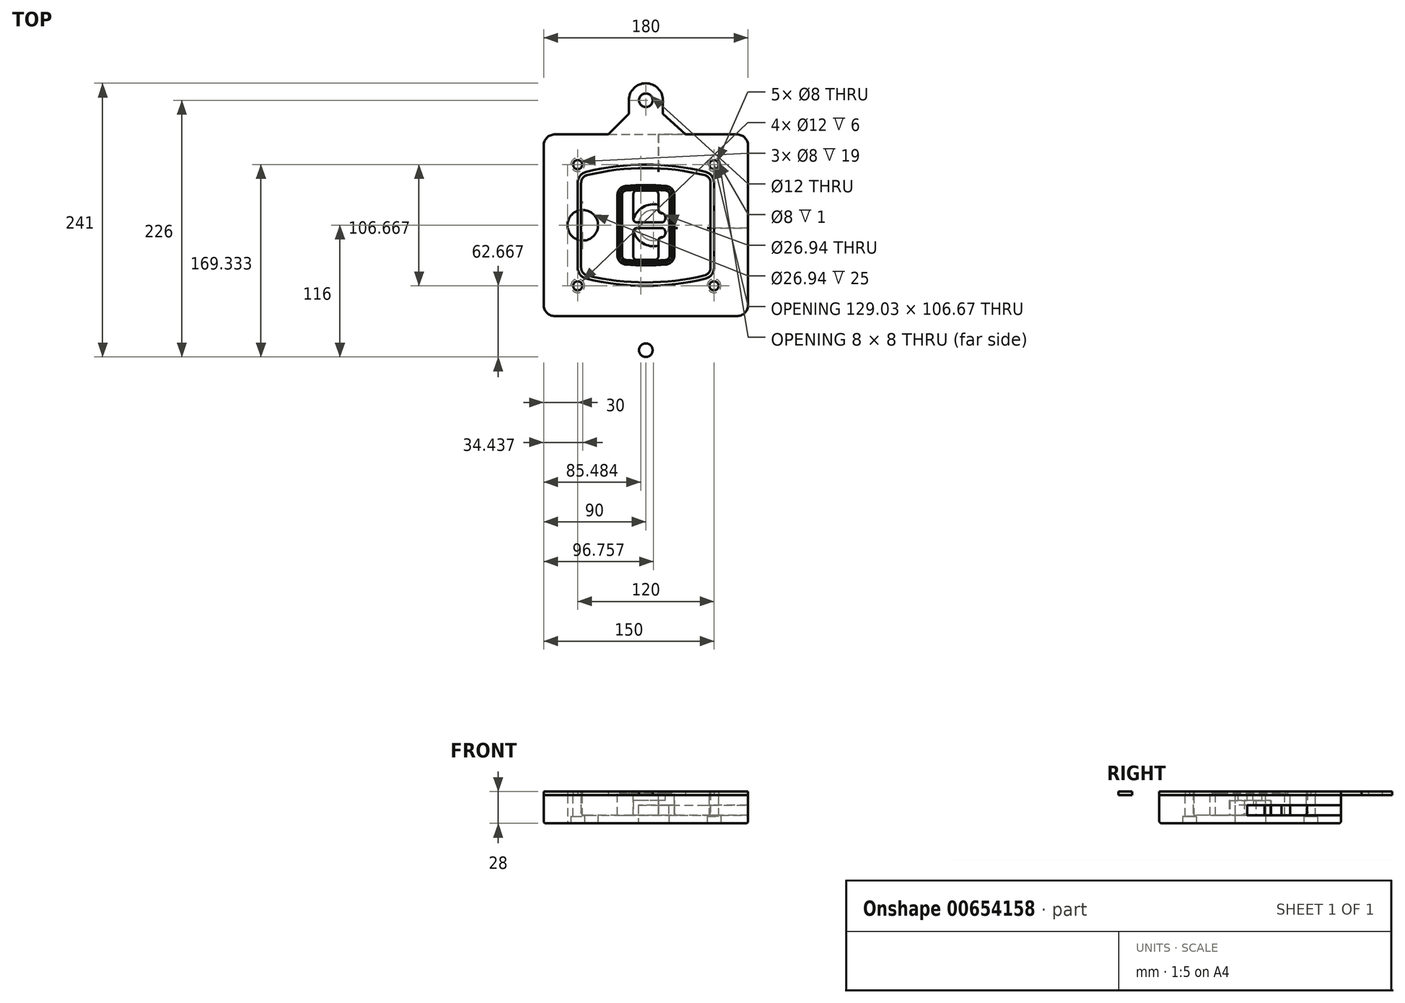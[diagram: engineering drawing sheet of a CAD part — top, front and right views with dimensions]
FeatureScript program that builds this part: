
annotation { "Feature Type Name" : "Feature", "Feature Type Description" : "" }
export const myFeature = defineFeature(function(context is Context, id is Id, definition is map)
    precondition{}
    {
        {
            var Q0;
            Q0=qCreatedBy(makeId("Top.planeOp"),FACE);
            var sketch = newSketch(context, id + "F0", { "sketchPlane" : qUnion([Q0])});
            skPoint(sketch, "E0.rect.middle", {"position": v(0, 0) * mm});
            skLineSegment(sketch, "E1.bottom", {"start": v(-80, -80) * mm, "end": v(80, -80) * mm});
            skLineSegment(sketch, "E1.top", {"start": v(-80, 80) * mm, "end": v(80, 80) * mm});
            skLineSegment(sketch, "E1.left", {"start": v(-90, -70) * mm, "end": v(-90, 70) * mm});
            skLineSegment(sketch, "E1.right", {"start": v(90, -70) * mm, "end": v(90, 70) * mm});
            skLineSegment(sketch, "E2", {"start": v(-90, 80) * mm, "end": v(90, -80) * mm, "construction": true});
            skLineSegment(sketch, "E3", {"start": v(90, 80) * mm, "end": v(-90, -80) * mm, "construction": true});
            skCircle(sketch, "E4", {"center": v(-60, 53.33) * mm, "radius": 4 * mm});
            skCircle(sketch, "E5", {"center": v(60, 53.33) * mm, "radius": 4 * mm});
            skCircle(sketch, "E6", {"center": v(60, -53.33) * mm, "radius": 4 * mm});
            skCircle(sketch, "E7", {"center": v(-60, -53.33) * mm, "radius": 4 * mm});
            skLineSegment(sketch, "E8", {"start": v(-60, 53.33) * mm, "end": v(60, 53.33) * mm, "construction": true});
            skLineSegment(sketch, "E9", {"start": v(60, 53.33) * mm, "end": v(60, -53.33) * mm, "construction": true});
            skLineSegment(sketch, "E10", {"start": v(60, -53.33) * mm, "end": v(-60, -53.33) * mm, "construction": true});
            skLineSegment(sketch, "E11", {"start": v(-60, -53.33) * mm, "end": v(-60, 53.33) * mm, "construction": true});
            skLineSegment(sketch, "E12", {"start": v(-60, 37.3) * mm, "end": v(-60, -37.3) * mm});
            skLineSegment(sketch, "E13", {"start": v(60, 37.3) * mm, "end": v(60, -37.3) * mm});
            skArc(sketch, "E14", {"start": v(52.38, 47.01) * mm, "mid": v(0, 53.33) * mm, "end": v(-52.38, 47.01) * mm});
            skArc(sketch, "E15", {"start": v(-52.38, -47.01) * mm, "mid": v(0, -53.33) * mm, "end": v(52.38, -47.01) * mm});
            skLineSegment(sketch, "E16", {"start": v(-60, 0) * mm, "end": v(60, 0) * mm, "construction": true});
            skPoint(sketch, "E17.visualSharp", {"position": v(-60, -45) * mm});
            skArc(sketch, "E17.filletArc", {"start": v(-60, -37.3) * mm, "mid": v(-57.87, -43.47) * mm, "end": v(-52.38, -47.01) * mm});
            skPoint(sketch, "E18.visualSharp", {"position": v(-60, 45) * mm});
            skArc(sketch, "E18.filletArc", {"start": v(-52.38, 47.01) * mm, "mid": v(-57.87, 43.47) * mm, "end": v(-60, 37.3) * mm});
            skPoint(sketch, "E19.visualSharp", {"position": v(60, 45) * mm});
            skArc(sketch, "E19.filletArc", {"start": v(60, 37.3) * mm, "mid": v(57.87, 43.47) * mm, "end": v(52.38, 47.01) * mm});
            skPoint(sketch, "E20.visualSharp", {"position": v(60, -45) * mm});
            skArc(sketch, "E20.filletArc", {"start": v(52.38, -47.01) * mm, "mid": v(57.87, -43.47) * mm, "end": v(60, -37.3) * mm});
            skPoint(sketch, "E21.visualSharp", {"position": v(-90, 80) * mm});
            skArc(sketch, "E21.filletArc", {"start": v(-80, 80) * mm, "mid": v(-87.07, 77.07) * mm, "end": v(-90, 70) * mm});
            skPoint(sketch, "E22.visualSharp", {"position": v(90, 80) * mm});
            skArc(sketch, "E22.filletArc", {"start": v(90, 70) * mm, "mid": v(87.07, 77.07) * mm, "end": v(80, 80) * mm});
            skPoint(sketch, "E23.visualSharp", {"position": v(90, -80) * mm});
            skArc(sketch, "E23.filletArc", {"start": v(80, -80) * mm, "mid": v(87.07, -77.07) * mm, "end": v(90, -70) * mm});
            skPoint(sketch, "E24.visualSharp", {"position": v(-90, -80) * mm});
            skArc(sketch, "E24.filletArc", {"start": v(-90, -70) * mm, "mid": v(-87.07, -77.07) * mm, "end": v(-80, -80) * mm});
            skArc(sketch, "E25.0", {"start": v(57, 37.3) * mm, "mid": v(55.5, 41.62) * mm, "end": v(51.67, 44.1) * mm});
            skLineSegment(sketch, "E25.1", {"start": v(57, 37.3) * mm, "end": v(57, -37.3) * mm});
            skArc(sketch, "E25.2", {"start": v(51.67, -44.1) * mm, "mid": v(55.5, -41.62) * mm, "end": v(57, -37.3) * mm});
            skArc(sketch, "E25.3", {"start": v(-51.67, -44.1) * mm, "mid": v(0, -50.33) * mm, "end": v(51.67, -44.1) * mm});
            skArc(sketch, "E25.4", {"start": v(-57, -37.3) * mm, "mid": v(-55.5, -41.62) * mm, "end": v(-51.67, -44.1) * mm});
            skArc(sketch, "E25.5", {"start": v(51.67, 44.1) * mm, "mid": v(0, 50.33) * mm, "end": v(-51.67, 44.1) * mm});
            skLineSegment(sketch, "E25.6", {"start": v(-57, 37.3) * mm, "end": v(-57, -37.3) * mm});
            skArc(sketch, "E25.7", {"start": v(-51.67, 44.1) * mm, "mid": v(-55.5, 41.62) * mm, "end": v(-57, 37.3) * mm});
            skArc(sketch, "E26.0", {"start": v(-53.33, 50.9) * mm, "mid": v(-61.01, 45.94) * mm, "end": v(-64, 37.3) * mm});
            skArc(sketch, "E26.1", {"start": v(53.33, 50.9) * mm, "mid": v(0, 57.33) * mm, "end": v(-53.33, 50.9) * mm});
            skArc(sketch, "E26.2", {"start": v(64, 37.3) * mm, "mid": v(61.01, 45.94) * mm, "end": v(53.33, 50.9) * mm});
            skLineSegment(sketch, "E26.3", {"start": v(64, 37.3) * mm, "end": v(64, -37.3) * mm});
            skArc(sketch, "E26.4", {"start": v(53.33, -50.9) * mm, "mid": v(61.01, -45.94) * mm, "end": v(64, -37.3) * mm});
            skLineSegment(sketch, "E26.5", {"start": v(-64, 37.3) * mm, "end": v(-64, -37.3) * mm});
            skArc(sketch, "E26.6", {"start": v(-53.33, -50.9) * mm, "mid": v(0, -57.33) * mm, "end": v(53.33, -50.9) * mm});
            skArc(sketch, "E26.7", {"start": v(-64, -37.3) * mm, "mid": v(-61.01, -45.94) * mm, "end": v(-53.33, -50.9) * mm});
            skSolve(sketch);
        }
        {
            var Q0;
            Q0=makeQuery(id+"F0.imprint","IMPRINT",FACE,{"disambiguationData":[TD([[makeQuery(id+"F0.imprint","IMPRINT",EDGE,{"derivedFrom":sQuery(id+"F0.wireOp",EDGE,"E1.bottom")}),1.0]])]});
            var Q1;
            Q1=makeQuery(id+"F0.imprint","IMPRINT",FACE,{"disambiguationData":[TD([[makeQuery(id+"F0.imprint","IMPRINT",EDGE,{"derivedFrom":sQuery(id+"F0.wireOp",EDGE,"E12")}),1.0]])]});
            var Q2;
            Q2=makeQuery(id+"F0.imprint","IMPRINT",FACE,{"disambiguationData":[TD([[makeQuery(id+"F0.imprint","IMPRINT",EDGE,{"derivedFrom":sQuery(id+"F0.wireOp",EDGE,"E25.0")}),1.0]])]});
            var Q3;
            Q3=makeQuery(id+"F0.imprint","IMPRINT",FACE,{"disambiguationData":[TD([[makeQuery(id+"F0.imprint","IMPRINT",EDGE,{"derivedFrom":sQuery(id+"F0.wireOp",EDGE,"E12")}),-1.0]])]});
            extrude(context, id + "F1", {"entities" : qUnion([Q0, Q1, Q2, Q3]), "oppositeDirection" : true, "depth" : 25 * mm});
        }
        {
            var Q0;
            Q0=makeQuery(id+"F0.imprint","IMPRINT",FACE,{"disambiguationData":[TD([[makeQuery(id+"F0.imprint","IMPRINT",EDGE,{"derivedFrom":sQuery(id+"F0.wireOp",EDGE,"E12")}),1.0]])]});
            extrude(context, id + "F2", {"entities" : qUnion([Q0]), "operationType" : NewBodyOperationType.ADD, "depth" : 3 * mm});
        }
        {
            var Q0;
            Q0=makeQuery(id+"F0.imprint","IMPRINT",FACE,{"disambiguationData":[TD([[makeQuery(id+"F0.imprint","IMPRINT",EDGE,{"derivedFrom":sQuery(id+"F0.wireOp",EDGE,"E25.0")}),1.0]])]});
            extrude(context, id + "F3", {"entities" : qUnion([Q0]), "operationType" : NewBodyOperationType.REMOVE, "oppositeDirection" : true, "depth" : 18 * mm});
        }
        {
            var Q0;
            Q0=makeQuery(id+"F2.opExtrude","CAP_FACE",FACE,{"disambiguationData":[OSD([sQuery(id+"F0.wireOp",EDGE,"E12"),sQuery(id+"F0.wireOp",EDGE,"E13"),sQuery(id+"F0.wireOp",EDGE,"E14"),sQuery(id+"F0.wireOp",EDGE,"E15"),sQuery(id+"F0.wireOp",EDGE,"E17.filletArc"),sQuery(id+"F0.wireOp",EDGE,"E18.filletArc"),sQuery(id+"F0.wireOp",EDGE,"E19.filletArc"),sQuery(id+"F0.wireOp",EDGE,"E20.filletArc"),sQuery(id+"F0.wireOp",EDGE,"E25.0"),sQuery(id+"F0.wireOp",EDGE,"E25.1"),sQuery(id+"F0.wireOp",EDGE,"E25.2"),sQuery(id+"F0.wireOp",EDGE,"E25.3"),sQuery(id+"F0.wireOp",EDGE,"E25.4"),sQuery(id+"F0.wireOp",EDGE,"E25.5"),sQuery(id+"F0.wireOp",EDGE,"E25.6"),sQuery(id+"F0.wireOp",EDGE,"E25.7")])],"isStart":false});
            var sketch = newSketch(context, id + "F4", { "sketchPlane" : qUnion([Q0])});
            skArc(sketch, "E27.0", {"start": v(-17.7, -34.56) * mm, "mid": v(0, -35.33) * mm, "end": v(17.7, -34.56) * mm});
            skArc(sketch, "E28.0", {"start": v(17.7, 34.56) * mm, "mid": v(0, 35.33) * mm, "end": v(-17.7, 34.56) * mm});
            skLineSegment(sketch, "E29", {"start": v(-25, 26.59) * mm, "end": v(-25, -26.59) * mm});
            skLineSegment(sketch, "E30", {"start": v(25, 26.59) * mm, "end": v(25, -26.59) * mm});
            skLineSegment(sketch, "E31", {"start": v(-25, 33.78) * mm, "end": v(25, 33.78) * mm, "construction": true});
            skLineSegment(sketch, "E32", {"start": v(-25, -33.78) * mm, "end": v(25, -33.78) * mm, "construction": true});
            skPoint(sketch, "E33.visualSharp", {"position": v(-25, 33.78) * mm});
            skArc(sketch, "E33.filletArc", {"start": v(-17.7, 34.56) * mm, "mid": v(-22.9, 32) * mm, "end": v(-25, 26.59) * mm});
            skPoint(sketch, "E34.visualSharp", {"position": v(25, 33.78) * mm});
            skArc(sketch, "E34.filletArc", {"start": v(25, 26.59) * mm, "mid": v(22.9, 32) * mm, "end": v(17.7, 34.56) * mm});
            skPoint(sketch, "E35.visualSharp", {"position": v(25, -33.78) * mm});
            skArc(sketch, "E35.filletArc", {"start": v(17.7, -34.56) * mm, "mid": v(22.9, -32) * mm, "end": v(25, -26.59) * mm});
            skPoint(sketch, "E36.visualSharp", {"position": v(-25, -33.78) * mm});
            skArc(sketch, "E36.filletArc", {"start": v(-25, -26.59) * mm, "mid": v(-22.9, -32) * mm, "end": v(-17.7, -34.56) * mm});
            skArc(sketch, "E37.0", {"start": v(51.67, 44.1) * mm, "mid": v(0, 50.33) * mm, "end": v(-51.67, 44.1) * mm});
            skArc(sketch, "E37.1", {"start": v(-51.67, 44.1) * mm, "mid": v(-55.5, 41.62) * mm, "end": v(-57, 37.3) * mm});
            skLineSegment(sketch, "E37.2", {"start": v(-57, 37.3) * mm, "end": v(-57, -37.3) * mm});
            skArc(sketch, "E37.3", {"start": v(-57, -37.3) * mm, "mid": v(-55.5, -41.62) * mm, "end": v(-51.67, -44.1) * mm});
            skArc(sketch, "E37.4", {"start": v(-51.67, -44.1) * mm, "mid": v(0, -50.33) * mm, "end": v(51.67, -44.1) * mm});
            skArc(sketch, "E37.5", {"start": v(51.67, -44.1) * mm, "mid": v(55.5, -41.62) * mm, "end": v(57, -37.3) * mm});
            skLineSegment(sketch, "E37.6", {"start": v(57, 37.3) * mm, "end": v(57, -37.3) * mm});
            skArc(sketch, "E37.7", {"start": v(57, 37.3) * mm, "mid": v(55.5, 41.62) * mm, "end": v(51.67, 44.1) * mm});
            skLineSegment(sketch, "E38.0", {"start": v(23, 26.59) * mm, "end": v(23, -26.59) * mm});
            skArc(sketch, "E38.1", {"start": v(17.53, -32.56) * mm, "mid": v(21.42, -30.64) * mm, "end": v(23, -26.59) * mm});
            skArc(sketch, "E38.2", {"start": v(-17.53, -32.56) * mm, "mid": v(0, -33.33) * mm, "end": v(17.53, -32.56) * mm});
            skArc(sketch, "E38.3", {"start": v(-23, -26.59) * mm, "mid": v(-21.42, -30.64) * mm, "end": v(-17.53, -32.56) * mm});
            skLineSegment(sketch, "E38.4", {"start": v(-23, 26.59) * mm, "end": v(-23, -26.59) * mm});
            skArc(sketch, "E38.5", {"start": v(23, 26.59) * mm, "mid": v(21.42, 30.64) * mm, "end": v(17.53, 32.56) * mm});
            skArc(sketch, "E38.6", {"start": v(-17.53, 32.56) * mm, "mid": v(-21.42, 30.64) * mm, "end": v(-23, 26.59) * mm});
            skArc(sketch, "E38.7", {"start": v(17.53, 32.56) * mm, "mid": v(0, 33.33) * mm, "end": v(-17.53, 32.56) * mm});
            skArc(sketch, "E39.0", {"start": v(21, 26.59) * mm, "mid": v(19.95, 29.29) * mm, "end": v(17.35, 30.57) * mm});
            skLineSegment(sketch, "E39.1", {"start": v(21, 26.59) * mm, "end": v(21, -26.59) * mm});
            skArc(sketch, "E39.2", {"start": v(17.35, -30.57) * mm, "mid": v(19.95, -29.29) * mm, "end": v(21, -26.59) * mm});
            skArc(sketch, "E39.3", {"start": v(-17.35, -30.57) * mm, "mid": v(0, -31.33) * mm, "end": v(17.35, -30.57) * mm});
            skArc(sketch, "E39.4", {"start": v(-21, -26.59) * mm, "mid": v(-19.95, -29.29) * mm, "end": v(-17.35, -30.57) * mm});
            skArc(sketch, "E39.5", {"start": v(17.35, 30.57) * mm, "mid": v(0, 31.33) * mm, "end": v(-17.35, 30.57) * mm});
            skLineSegment(sketch, "E39.6", {"start": v(-21, 26.59) * mm, "end": v(-21, -26.59) * mm});
            skArc(sketch, "E39.7", {"start": v(-17.35, 30.57) * mm, "mid": v(-19.95, 29.29) * mm, "end": v(-21, 26.59) * mm});
            skLineSegment(sketch, "E40", {"start": v(-25, 0) * mm, "end": v(25, 0) * mm, "construction": true});
            skLineSegment(sketch, "E41", {"start": v(-11, 5.5) * mm, "end": v(-11, 27.5) * mm});
            skLineSegment(sketch, "E42", {"start": v(-8, 30.5) * mm, "end": v(8, 30.5) * mm});
            skLineSegment(sketch, "E43", {"start": v(11, 27.5) * mm, "end": v(11, 13.5) * mm});
            skLineSegment(sketch, "E44", {"start": v(14, 10.5) * mm, "end": v(14, 10.5) * mm});
            skLineSegment(sketch, "E45", {"start": v(17, 7.5) * mm, "end": v(17, 5.5) * mm});
            skLineSegment(sketch, "E46", {"start": v(14, 2.5) * mm, "end": v(-8, 2.5) * mm});
            skPoint(sketch, "E47.visualSharp", {"position": v(-11, 30.5) * mm});
            skArc(sketch, "E47.filletArc", {"start": v(-8, 30.5) * mm, "mid": v(-10.12, 29.62) * mm, "end": v(-11, 27.5) * mm});
            skPoint(sketch, "E48.visualSharp", {"position": v(11, 30.5) * mm});
            skArc(sketch, "E48.filletArc", {"start": v(11, 27.5) * mm, "mid": v(10.12, 29.62) * mm, "end": v(8, 30.5) * mm});
            skPoint(sketch, "E49.visualSharp", {"position": v(11, 10.5) * mm});
            skArc(sketch, "E49.filletArc", {"start": v(11, 13.5) * mm, "mid": v(11.88, 11.38) * mm, "end": v(14, 10.5) * mm});
            skPoint(sketch, "E50.visualSharp", {"position": v(17, 10.5) * mm});
            skArc(sketch, "E50.filletArc", {"start": v(17, 7.5) * mm, "mid": v(16.12, 9.62) * mm, "end": v(14, 10.5) * mm});
            skPoint(sketch, "E51.visualSharp", {"position": v(17, 2.5) * mm});
            skArc(sketch, "E51.filletArc", {"start": v(14, 2.5) * mm, "mid": v(16.12, 3.38) * mm, "end": v(17, 5.5) * mm});
            skPoint(sketch, "E52.visualSharp", {"position": v(-11, 2.5) * mm});
            skArc(sketch, "E52.filletArc", {"start": v(-11, 5.5) * mm, "mid": v(-10.12, 3.38) * mm, "end": v(-8, 2.5) * mm});
            skLineSegment(sketch, "E53.0.MirrorCS", {"start": v(14, -2.5) * mm, "end": v(-8, -2.5) * mm});
            skArc(sketch, "E54.0.MirrorCS", {"start": v(-11, -5.5) * mm, "mid": v(-10.12, -3.38) * mm, "end": v(-8, -2.5) * mm});
            skLineSegment(sketch, "E55.0.MirrorCS", {"start": v(-11, -5.5) * mm, "end": v(-11, -27.5) * mm});
            skArc(sketch, "E56.0.MirrorCS", {"start": v(-8, -30.5) * mm, "mid": v(-10.12, -29.62) * mm, "end": v(-11, -27.5) * mm});
            skLineSegment(sketch, "E57.0.MirrorCS", {"start": v(-8, -30.5) * mm, "end": v(8, -30.5) * mm});
            skArc(sketch, "E58.0.MirrorCS", {"start": v(11, -27.5) * mm, "mid": v(10.12, -29.62) * mm, "end": v(8, -30.5) * mm});
            skLineSegment(sketch, "E59.0.MirrorCS", {"start": v(11, -27.5) * mm, "end": v(11, -13.5) * mm});
            skArc(sketch, "E60.0.MirrorCS", {"start": v(11, -13.5) * mm, "mid": v(11.88, -11.38) * mm, "end": v(14, -10.5) * mm});
            skArc(sketch, "E61.0.MirrorCS", {"start": v(17, -7.5) * mm, "mid": v(16.12, -9.62) * mm, "end": v(14, -10.5) * mm});
            skLineSegment(sketch, "E62.0.MirrorCS", {"start": v(17, -7.5) * mm, "end": v(17, -5.5) * mm});
            skArc(sketch, "E63.0.MirrorCS", {"start": v(14, -2.5) * mm, "mid": v(16.12, -3.38) * mm, "end": v(17, -5.5) * mm});
            skSolve(sketch);
        }
        {
            var Q0;
            Q0=makeQuery(id+"F4.imprint","IMPRINT",FACE,{"disambiguationData":[TD([[makeQuery(id+"F4.imprint","IMPRINT",EDGE,{"derivedFrom":sQuery(id+"F4.wireOp",EDGE,"E27.0")}),1.0]])]});
            var Q1;
            Q1=makeQuery(id+"F4.imprint","IMPRINT",FACE,{"disambiguationData":[TD([[makeQuery(id+"F4.imprint","IMPRINT",EDGE,{"derivedFrom":sQuery(id+"F4.wireOp",EDGE,"E38.0")}),-1.0]])]});
            var Q2;
            Q2=makeQuery(id+"F4.imprint","IMPRINT",FACE,{"disambiguationData":[TD([[makeQuery(id+"F4.imprint","IMPRINT",EDGE,{"derivedFrom":sQuery(id+"F4.wireOp",EDGE,"E39.0")}),1.0]])]});
            extrude(context, id + "F5", {"entities" : qUnion([Q0, Q1, Q2]), "operationType" : NewBodyOperationType.ADD, "endBound" : BoundingType.UP_TO_NEXT, "oppositeDirection" : true, "depth" : 25 * mm});
        }
        {
            var Q0;
            Q0=makeQuery(id+"F4.imprint","IMPRINT",FACE,{"disambiguationData":[TD([[makeQuery(id+"F4.imprint","IMPRINT",EDGE,{"derivedFrom":sQuery(id+"F4.wireOp",EDGE,"E38.0")}),-1.0]])]});
            extrude(context, id + "F6", {"entities" : qUnion([Q0]), "operationType" : NewBodyOperationType.REMOVE, "oppositeDirection" : true, "depth" : 2 * mm});
        }
        {
            var Q0;
            Q0=makeQuery(id+"F1.opExtrude","CAP_FACE",FACE,{"disambiguationData":[OSD([sQuery(id+"F0.wireOp",EDGE,"E1.bottom"),sQuery(id+"F0.wireOp",EDGE,"E1.top"),sQuery(id+"F0.wireOp",EDGE,"E1.left"),sQuery(id+"F0.wireOp",EDGE,"E1.right"),sQuery(id+"F0.wireOp",EDGE,"E4"),sQuery(id+"F0.wireOp",EDGE,"E5"),sQuery(id+"F0.wireOp",EDGE,"E6"),sQuery(id+"F0.wireOp",EDGE,"E7"),sQuery(id+"F0.wireOp",EDGE,"E21.filletArc"),sQuery(id+"F0.wireOp",EDGE,"E22.filletArc"),sQuery(id+"F0.wireOp",EDGE,"E23.filletArc"),sQuery(id+"F0.wireOp",EDGE,"E24.filletArc")])],"isStart":false});
            var sketch = newSketch(context, id + "F7", { "sketchPlane" : qUnion([Q0])});
            skCircle(sketch, "E64", {"center": v(6.76, 0) * mm, "radius": 13.47 * mm});
            skCircle(sketch, "E65", {"center": v(-55.56, 0) * mm, "radius": 13.47 * mm});
            skLineSegment(sketch, "E66", {"start": v(90, 0) * mm, "end": v(-90, 0) * mm});
            skCircle(sketch, "E67", {"center": v(6.76, 0) * mm, "radius": 18.47 * mm});
            skCircle(sketch, "E68", {"center": v(60, -53.33) * mm, "radius": 6 * mm});
            skCircle(sketch, "E69", {"center": v(-60, -53.33) * mm, "radius": 6 * mm});
            skCircle(sketch, "E70", {"center": v(-60, 53.33) * mm, "radius": 6 * mm});
            skCircle(sketch, "E71", {"center": v(60, 53.33) * mm, "radius": 6 * mm});
            skSolve(sketch);
        }
        {
            var Q0;
            {var subQ1=sQuery(id+"F7.wireOp",EDGE,"E66");var subQ4=sQuery(id+"F7.wireOp",EDGE,"E64");var subQ6=makeQuery(id+"F7.imprint","INTERSECT",VERTEX,{"disambiguationData":[OD(0.0)],"derivedFrom":[subQ4,subQ1]});Q0=makeQuery(id+"F7.imprint","IMPRINT",FACE,{"disambiguationData":[TD([[makeQuery(id+"F7.imprint","IMPRINT",EDGE,{"disambiguationData":[TD([[subQ6,-1.0]])],"derivedFrom":subQ4}),-1.0]])]});}
            var Q1;
            {var subQ0=sQuery(id+"F7.wireOp",EDGE,"E66");var subQ1=sQuery(id+"F7.wireOp",EDGE,"E64");var subQ3=makeQuery(id+"F7.imprint","INTERSECT",VERTEX,{"disambiguationData":[OD(0.0)],"derivedFrom":[subQ1,subQ0]});Q1=makeQuery(id+"F7.imprint","IMPRINT",FACE,{"disambiguationData":[TD([[makeQuery(id+"F7.imprint","IMPRINT",EDGE,{"disambiguationData":[TD([[subQ3,-1.0]])],"derivedFrom":subQ1}),1.0]])]});}
            var Q2;
            {var subQ0=sQuery(id+"F7.wireOp",EDGE,"E66");var subQ1=sQuery(id+"F7.wireOp",EDGE,"E64");var subQ3=makeQuery(id+"F7.imprint","INTERSECT",VERTEX,{"disambiguationData":[OD(0.0)],"derivedFrom":[subQ1,subQ0]});Q2=makeQuery(id+"F7.imprint","IMPRINT",FACE,{"disambiguationData":[TD([[makeQuery(id+"F7.imprint","IMPRINT",EDGE,{"disambiguationData":[TD([[subQ3,1.0]])],"derivedFrom":subQ1}),1.0]])]});}
            var Q3;
            {var subQ1=sQuery(id+"F7.wireOp",EDGE,"E66");var subQ4=sQuery(id+"F7.wireOp",EDGE,"E64");var subQ6=makeQuery(id+"F7.imprint","INTERSECT",VERTEX,{"disambiguationData":[OD(0.0)],"derivedFrom":[subQ4,subQ1]});Q3=makeQuery(id+"F7.imprint","IMPRINT",FACE,{"disambiguationData":[TD([[makeQuery(id+"F7.imprint","IMPRINT",EDGE,{"disambiguationData":[TD([[subQ6,1.0]])],"derivedFrom":subQ4}),-1.0]])]});}
            extrude(context, id + "F8", {"entities" : qUnion([Q0, Q1, Q2, Q3]), "operationType" : NewBodyOperationType.ADD, "oppositeDirection" : true, "depth" : 20 * mm});
        }
        {
            var Q0;
            {var subQ0=sQuery(id+"F7.wireOp",EDGE,"E66");var subQ1=sQuery(id+"F7.wireOp",EDGE,"E64");var subQ3=makeQuery(id+"F7.imprint","INTERSECT",VERTEX,{"disambiguationData":[OD(0.0)],"derivedFrom":[subQ1,subQ0]});Q0=makeQuery(id+"F7.imprint","IMPRINT",FACE,{"disambiguationData":[TD([[makeQuery(id+"F7.imprint","IMPRINT",EDGE,{"disambiguationData":[TD([[subQ3,-1.0]])],"derivedFrom":subQ1}),1.0]])]});}
            var Q1;
            {var subQ0=sQuery(id+"F7.wireOp",EDGE,"E66");var subQ1=sQuery(id+"F7.wireOp",EDGE,"E64");var subQ3=makeQuery(id+"F7.imprint","INTERSECT",VERTEX,{"disambiguationData":[OD(0.0)],"derivedFrom":[subQ1,subQ0]});Q1=makeQuery(id+"F7.imprint","IMPRINT",FACE,{"disambiguationData":[TD([[makeQuery(id+"F7.imprint","IMPRINT",EDGE,{"disambiguationData":[TD([[subQ3,1.0]])],"derivedFrom":subQ1}),1.0]])]});}
            extrude(context, id + "F9", {"entities" : qUnion([Q0, Q1]), "operationType" : NewBodyOperationType.REMOVE, "oppositeDirection" : true, "depth" : 16 * mm});
        }
        {
            var Q0;
            {var subQ0=sQuery(id+"F7.wireOp",EDGE,"E66");var subQ1=sQuery(id+"F7.wireOp",EDGE,"E65");var subQ3=makeQuery(id+"F7.imprint","INTERSECT",VERTEX,{"disambiguationData":[OD(0.0)],"derivedFrom":[subQ1,subQ0]});Q0=makeQuery(id+"F7.imprint","IMPRINT",FACE,{"disambiguationData":[TD([[makeQuery(id+"F7.imprint","IMPRINT",EDGE,{"disambiguationData":[TD([[subQ3,-1.0]])],"derivedFrom":subQ1}),1.0]])]});}
            var Q1;
            {var subQ0=sQuery(id+"F7.wireOp",EDGE,"E66");var subQ1=sQuery(id+"F7.wireOp",EDGE,"E65");var subQ3=makeQuery(id+"F7.imprint","INTERSECT",VERTEX,{"disambiguationData":[OD(0.0)],"derivedFrom":[subQ1,subQ0]});Q1=makeQuery(id+"F7.imprint","IMPRINT",FACE,{"disambiguationData":[TD([[makeQuery(id+"F7.imprint","IMPRINT",EDGE,{"disambiguationData":[TD([[subQ3,1.0]])],"derivedFrom":subQ1}),1.0]])]});}
            extrude(context, id + "F10", {"entities" : qUnion([Q0, Q1]), "operationType" : NewBodyOperationType.REMOVE, "oppositeDirection" : true, "depth" : 25 * mm});
        }
        {
            var Q0;
            Q0=makeQuery(id+"F7.imprint","IMPRINT",FACE,{"disambiguationData":[TD([[makeQuery(id+"F7.imprint","IMPRINT",EDGE,{"derivedFrom":sQuery(id+"F7.wireOp",EDGE,"E68")}),1.0]])]});
            var Q1;
            Q1=makeQuery(id+"F7.imprint","IMPRINT",FACE,{"disambiguationData":[TD([[makeQuery(id+"F7.imprint","IMPRINT",EDGE,{"derivedFrom":makeQuery(id+"F1.opExtrude","CAP_EDGE",EDGE,{"disambiguationData":[OSD([sQuery(id+"F0.wireOp",EDGE,"E5")])],"isStart":false})}),-1.0]])]});
            var Q2;
            Q2=makeQuery(id+"F7.imprint","IMPRINT",FACE,{"disambiguationData":[TD([[makeQuery(id+"F7.imprint","IMPRINT",EDGE,{"derivedFrom":sQuery(id+"F7.wireOp",EDGE,"E69")}),1.0]])]});
            var Q3;
            Q3=makeQuery(id+"F7.imprint","IMPRINT",FACE,{"disambiguationData":[TD([[makeQuery(id+"F7.imprint","IMPRINT",EDGE,{"derivedFrom":makeQuery(id+"F1.opExtrude","CAP_EDGE",EDGE,{"disambiguationData":[OSD([sQuery(id+"F0.wireOp",EDGE,"E4")])],"isStart":false})}),-1.0]])]});
            var Q4;
            Q4=makeQuery(id+"F7.imprint","IMPRINT",FACE,{"disambiguationData":[TD([[makeQuery(id+"F7.imprint","IMPRINT",EDGE,{"derivedFrom":sQuery(id+"F7.wireOp",EDGE,"E70")}),1.0]])]});
            var Q5;
            Q5=makeQuery(id+"F7.imprint","IMPRINT",FACE,{"disambiguationData":[TD([[makeQuery(id+"F7.imprint","IMPRINT",EDGE,{"derivedFrom":makeQuery(id+"F1.opExtrude","CAP_EDGE",EDGE,{"disambiguationData":[OSD([sQuery(id+"F0.wireOp",EDGE,"E7")])],"isStart":false})}),-1.0]])]});
            var Q6;
            Q6=makeQuery(id+"F7.imprint","IMPRINT",FACE,{"disambiguationData":[TD([[makeQuery(id+"F7.imprint","IMPRINT",EDGE,{"derivedFrom":sQuery(id+"F7.wireOp",EDGE,"E71")}),1.0]])]});
            var Q7;
            Q7=makeQuery(id+"F7.imprint","IMPRINT",FACE,{"disambiguationData":[TD([[makeQuery(id+"F7.imprint","IMPRINT",EDGE,{"derivedFrom":makeQuery(id+"F1.opExtrude","CAP_EDGE",EDGE,{"disambiguationData":[OSD([sQuery(id+"F0.wireOp",EDGE,"E6")])],"isStart":false})}),-1.0]])]});
            extrude(context, id + "F11", {"entities" : qUnion([Q0, Q1, Q2, Q3, Q4, Q5, Q6, Q7]), "operationType" : NewBodyOperationType.REMOVE, "oppositeDirection" : true, "depth" : 6 * mm});
        }
        {
            var Q0;
            Q0=makeQuery(id+"F9.boolean.opBoolean","COPY",FACE,{"derivedFrom":makeQuery(id+"F9.opExtrude","CAP_FACE",FACE,{"disambiguationData":[OSD([sQuery(id+"F7.wireOp",EDGE,"E64")])],"isStart":false})});
            var sketch = newSketch(context, id + "F12", { "sketchPlane" : qUnion([Q0])});
            skArc(sketch, "E72.0", {"start": v(11, -88.19) * mm, "mid": v(97.1, -83.6) * mm, "end": v(92.5, 2.5) * mm});
            skLineSegment(sketch, "E72.1", {"start": v(11, -17.97) * mm, "end": v(11, -17.97) * mm});
            skLineSegment(sketch, "E73", {"start": v(92.5, -105.13) * mm, "end": v(102.3, -105.13) * mm});
            skLineSegment(sketch, "E74.0", {"start": v(92.5, 2.5) * mm, "end": v(14, 2.5) * mm});
            skArc(sketch, "E74.1", {"start": v(14, 2.5) * mm, "mid": v(16.12, 3.38) * mm, "end": v(17, 5.5) * mm});
            skLineSegment(sketch, "E74.2", {"start": v(17, 7.5) * mm, "end": v(17, 5.5) * mm});
            skArc(sketch, "E74.3", {"start": v(17, 7.5) * mm, "mid": v(16.12, 9.62) * mm, "end": v(14, 10.5) * mm});
            skArc(sketch, "E74.4", {"start": v(11, 13.5) * mm, "mid": v(11.88, 11.38) * mm, "end": v(14, 10.5) * mm});
            skLineSegment(sketch, "E74.5", {"start": v(11, 13.5) * mm, "end": v(11, -88.19) * mm});
            skLineSegment(sketch, "E74.7", {"start": v(92.5, -2.5) * mm, "end": v(14, -2.5) * mm});
            skArc(sketch, "E74.8", {"start": v(14, -2.5) * mm, "mid": v(16.12, -3.38) * mm, "end": v(17, -5.5) * mm});
            skLineSegment(sketch, "E74.9", {"start": v(17, -7.5) * mm, "end": v(17, -5.5) * mm});
            skArc(sketch, "E74.10", {"start": v(17, -7.5) * mm, "mid": v(16.12, -9.62) * mm, "end": v(14, -10.5) * mm});
            skArc(sketch, "E74.11", {"start": v(11, -13.5) * mm, "mid": v(11.88, -11.38) * mm, "end": v(14, -10.5) * mm});
            skLineSegment(sketch, "E74.12", {"start": v(11, -17.97) * mm, "end": v(11, -13.5) * mm});
            skPoint(sketch, "E75.orphan", {"position": v(11, -27.5) * mm});
            skPoint(sketch, "E76.orphan", {"position": v(-8, -2.5) * mm});
            skPoint(sketch, "E77.orphan", {"position": v(-8, 2.5) * mm});
            skPoint(sketch, "E78.orphan", {"position": v(11, 27.5) * mm});
            skSolve(sketch);
        }
        {
            var Q0;
            {var subQ7=sQuery(id+"F12.wireOp",EDGE,"E72.0");var subQ14=sQuery(id+"F12.wireOp",EDGE,"E72.1");var subQ16=sQuery(id+"F12.wireOp",EDGE,"E74.1");var subQ18=sQuery(id+"F12.wireOp",EDGE,"E74.8");Q0=qUnion([makeQuery(id+"F12.imprint","IMPRINT",FACE,{"disambiguationData":[TD([[makeQuery(id+"F12.imprint","IMPRINT",EDGE,{"derivedFrom":subQ7}),1.0]])]}),makeQuery(id+"F12.imprint","IMPRINT",FACE,{"disambiguationData":[TD([[makeQuery(id+"F12.imprint","IMPRINT",EDGE,{"derivedFrom":subQ14}),1.0]])]}),makeQuery(id+"F12.imprint","IMPRINT",FACE,{"disambiguationData":[TD([[makeQuery(id+"F12.imprint","IMPRINT",EDGE,{"derivedFrom":subQ16}),1.0]])]}),makeQuery(id+"F12.imprint","IMPRINT",FACE,{"disambiguationData":[TD([[makeQuery(id+"F12.imprint","IMPRINT",EDGE,{"derivedFrom":subQ18}),-1.0]])]})]);}
            var Q1;
            Q1=makeQuery(id+"F5.boolean.opBoolean","SPLIT",FACE,{"disambiguationData":[TD([makeQuery(id+"F5.opExtrude","SWEPT_FACE",FACE,{"disambiguationData":[OSD([sQuery(id+"F4.wireOp",EDGE,"E41")])]})])],"derivedFrom":makeQuery(id+"F3.boolean.opBoolean","COPY",FACE,{"derivedFrom":makeQuery(id+"F3.opExtrude","CAP_FACE",FACE,{"disambiguationData":[OSD([sQuery(id+"F0.wireOp",EDGE,"E25.0"),sQuery(id+"F0.wireOp",EDGE,"E25.1"),sQuery(id+"F0.wireOp",EDGE,"E25.2"),sQuery(id+"F0.wireOp",EDGE,"E25.3"),sQuery(id+"F0.wireOp",EDGE,"E25.4"),sQuery(id+"F0.wireOp",EDGE,"E25.5"),sQuery(id+"F0.wireOp",EDGE,"E25.6"),sQuery(id+"F0.wireOp",EDGE,"E25.7")])],"isStart":false})})});
            extrude(context, id + "F13", {"entities" : qUnion([Q0]), "operationType" : NewBodyOperationType.REMOVE, "endBound" : BoundingType.UP_TO_SURFACE, "endBoundEntityFace" : qUnion([Q1]), "depth" : 25 * mm});
        }
        {
            var Q0;
            Q0=makeQuery(id+"F3.boolean.opBoolean","COPY",EDGE,{"derivedFrom":makeQuery(id+"F3.opExtrude","CAP_EDGE",EDGE,{"disambiguationData":[OSD([sQuery(id+"F0.wireOp",EDGE,"E25.6")])],"isStart":false})});
            var Q1;
            Q1=makeQuery(id+"F8.boolean.opBoolean","INTERSECT",EDGE,{"derivedFrom":[makeQuery(id+"F5.opExtrude","SWEPT_FACE",FACE,{"disambiguationData":[OSD([sQuery(id+"F4.wireOp",EDGE,"E30")])]}),makeQuery(id+"F8.opExtrude","CAP_FACE",FACE,{"disambiguationData":[OSD([sQuery(id+"F7.wireOp",EDGE,"E67")])],"isStart":false})]});
            var Q2;
            Q2=makeQuery(id+"F8.boolean.opBoolean","INTERSECT",EDGE,{"disambiguationData":[OD(1.0)],"derivedFrom":[makeQuery(id+"F5.opExtrude","SWEPT_FACE",FACE,{"disambiguationData":[OSD([sQuery(id+"F4.wireOp",EDGE,"E30")])]}),makeQuery(id+"F8.opExtrude","SWEPT_FACE",FACE,{"disambiguationData":[OSD([sQuery(id+"F7.wireOp",EDGE,"E67")])]})]});
            var Q3;
            {var subQ0=makeQuery(id+"F3.boolean.opBoolean","COPY",FACE,{"derivedFrom":makeQuery(id+"F3.opExtrude","CAP_FACE",FACE,{"disambiguationData":[OSD([sQuery(id+"F0.wireOp",EDGE,"E25.0"),sQuery(id+"F0.wireOp",EDGE,"E25.1"),sQuery(id+"F0.wireOp",EDGE,"E25.2"),sQuery(id+"F0.wireOp",EDGE,"E25.3"),sQuery(id+"F0.wireOp",EDGE,"E25.4"),sQuery(id+"F0.wireOp",EDGE,"E25.5"),sQuery(id+"F0.wireOp",EDGE,"E25.6"),sQuery(id+"F0.wireOp",EDGE,"E25.7")])],"isStart":false})});var subQ1=sQuery(id+"F4.wireOp",EDGE,"E30");Q3=makeQuery(id+"F8.boolean.opBoolean","SPLIT",EDGE,{"disambiguationData":[TD([makeQuery(id+"F5.opExtrude","SWEPT_FACE",FACE,{"disambiguationData":[OSD([sQuery(id+"F4.wireOp",EDGE,"E35.filletArc")])]})])],"derivedFrom":makeQuery(id+"F5.opExtrude","TWEAK_EDGE",EDGE,{"derivedFrom":[subQ0,makeQuery(id+"F4.imprint","IMPRINT",EDGE,{"derivedFrom":subQ1})]})});}
            var Q4;
            {var subQ0=sQuery(id+"F0.wireOp",EDGE,"E25.0");var subQ1=sQuery(id+"F0.wireOp",EDGE,"E25.1");var subQ2=sQuery(id+"F0.wireOp",EDGE,"E25.2");var subQ3=sQuery(id+"F0.wireOp",EDGE,"E25.3");var subQ4=sQuery(id+"F0.wireOp",EDGE,"E25.4");var subQ5=sQuery(id+"F0.wireOp",EDGE,"E25.5");var subQ6=sQuery(id+"F0.wireOp",EDGE,"E25.6");var subQ7=sQuery(id+"F0.wireOp",EDGE,"E25.7");Q4=makeQuery(id+"F8.boolean.opBoolean","INTERSECT",EDGE,{"derivedFrom":[makeQuery(id+"F5.boolean.opBoolean","SPLIT",FACE,{"disambiguationData":[TD([makeQuery(id+"F2.opExtrude","SWEPT_FACE",FACE,{"disambiguationData":[OSD([subQ0])]})])],"derivedFrom":makeQuery(id+"F3.boolean.opBoolean","COPY",FACE,{"derivedFrom":makeQuery(id+"F3.opExtrude","CAP_FACE",FACE,{"disambiguationData":[OSD([subQ0,subQ1,subQ2,subQ3,subQ4,subQ5,subQ6,subQ7])],"isStart":false})})}),makeQuery(id+"F8.opExtrude","SWEPT_FACE",FACE,{"disambiguationData":[OSD([sQuery(id+"F7.wireOp",EDGE,"E67")])]})]});}
            var Q5;
            Q5=makeQuery(id+"F8.boolean.opBoolean","INTERSECT",EDGE,{"disambiguationData":[OD(0.0)],"derivedFrom":[makeQuery(id+"F5.opExtrude","SWEPT_FACE",FACE,{"disambiguationData":[OSD([sQuery(id+"F4.wireOp",EDGE,"E30")])]}),makeQuery(id+"F8.opExtrude","SWEPT_FACE",FACE,{"disambiguationData":[OSD([sQuery(id+"F7.wireOp",EDGE,"E67")])]})]});
            fillet(context, id + "F14", {"entities" : qUnion([Q0, Q1, Q2, Q3, Q4, Q5]), "radius" : 3 * mm, "tangentPropagation" : true, "allowEdgeOverflow" : false});
        }
        {
            var Q0;
            Q0=makeQuery(id+"F1.opExtrude","CAP_EDGE",EDGE,{"disambiguationData":[OSD([sQuery(id+"F0.wireOp",EDGE,"E1.bottom")])],"isStart":false});
            fillet(context, id + "F15", {"entities" : qUnion([Q0]), "radius" : 2 * mm, "tangentPropagation" : true, "allowEdgeOverflow" : false});
        }
        {
            var Q0;
            {var subQ0=sQuery(id+"F0.wireOp",EDGE,"E21.filletArc");var subQ1=sQuery(id+"F0.wireOp",EDGE,"E7");var subQ2=sQuery(id+"F0.wireOp",EDGE,"E6");var subQ3=sQuery(id+"F0.wireOp",EDGE,"E5");var subQ4=sQuery(id+"F0.wireOp",EDGE,"E4");var subQ5=sQuery(id+"F0.wireOp",EDGE,"E22.filletArc");var subQ6=sQuery(id+"F0.wireOp",EDGE,"E1.bottom");var subQ7=sQuery(id+"F0.wireOp",EDGE,"E1.right");var subQ8=sQuery(id+"F0.wireOp",EDGE,"E1.top");var subQ9=sQuery(id+"F0.wireOp",EDGE,"E1.left");var subQ10=sQuery(id+"F0.wireOp",EDGE,"E23.filletArc");var subQ11=sQuery(id+"F0.wireOp",EDGE,"E24.filletArc");Q0=makeQuery(id+"F2.boolean.opBoolean","SPLIT",FACE,{"disambiguationData":[TD([makeQuery(id+"F1.opExtrude","SWEPT_FACE",FACE,{"disambiguationData":[OSD([subQ6])]})])],"derivedFrom":makeQuery(id+"F1.opExtrude","CAP_FACE",FACE,{"disambiguationData":[OSD([subQ6,subQ8,subQ9,subQ7,subQ4,subQ3,subQ2,subQ1,subQ0,subQ5,subQ10,subQ11])],"isStart":true})});}
            var sketch = newSketch(context, id + "F16", { "sketchPlane" : qUnion([Q0])});
            skLineSegment(sketch, "E79", {"start": v(0, 80) * mm, "end": v(0, 110) * mm, "construction": true});
            skCircle(sketch, "E80", {"center": v(0, 110) * mm, "radius": 6 * mm});
            skPoint(sketch, "E81", {"position": v(35, 80) * mm});
            skPoint(sketch, "E82", {"position": v(-33, 80) * mm});
            skLineSegment(sketch, "E83", {"start": v(-33, 80) * mm, "end": v(-15, 98) * mm});
            skLineSegment(sketch, "E84", {"start": v(-15, 98) * mm, "end": v(-15, 110) * mm});
            skLineSegment(sketch, "E85", {"start": v(35, 80) * mm, "end": v(15, 98) * mm});
            skLineSegment(sketch, "E86", {"start": v(15, 98) * mm, "end": v(15, 110) * mm});
            skArc(sketch, "E87", {"start": v(15, 110) * mm, "mid": v(0, 125) * mm, "end": v(-15, 110) * mm});
            skLineSegment(sketch, "E88", {"start": v(-90, 0) * mm, "end": v(90, 0) * mm, "construction": true});
            skArc(sketch, "E89.MirrorCS", {"start": v(15, -110) * mm, "mid": v(0, -125) * mm, "end": v(-15, -110) * mm});
            skLineSegment(sketch, "E90.MirrorCS", {"start": v(15, -98) * mm, "end": v(15, -110) * mm});
            skCircle(sketch, "E91.MirrorC", {"center": v(0, -110) * mm, "radius": 6 * mm});
            skLineSegment(sketch, "E92.MirrorCS", {"start": v(-15, -98) * mm, "end": v(-15, -110) * mm});
            skLineSegment(sketch, "E93.MirrorCS", {"start": v(0, -80) * mm, "end": v(0, -110) * mm, "construction": true});
            skLineSegment(sketch, "E94.MirrorCS", {"start": v(-33, -80) * mm, "end": v(-15, -98) * mm});
            skPoint(sketch, "E95.MirrorP", {"position": v(-33, -80) * mm});
            skPoint(sketch, "E96.MirrorP", {"position": v(35, -80) * mm});
            skLineSegment(sketch, "E97.MirrorCS", {"start": v(35, -80) * mm, "end": v(15, -98) * mm});
            skSolve(sketch);
        }
        {
            var Q0;
            Q0=makeQuery(id+"F16.imprint","IMPRINT",FACE,{"disambiguationData":[TD([[makeQuery(id+"F16.imprint","IMPRINT",EDGE,{"derivedFrom":makeQuery(id+"F1.opExtrude","CAP_EDGE",EDGE,{"disambiguationData":[OSD([sQuery(id+"F0.wireOp",EDGE,"E1.left")])],"isStart":true})}),-1.0]])]});
            var Q1;
            Q1=makeQuery(id+"F16.imprint","IMPRINT",FACE,{"disambiguationData":[TD([[makeQuery(id+"F16.imprint","IMPRINT",EDGE,{"derivedFrom":sQuery(id+"F16.wireOp",EDGE,"E80")}),-1.0]])]});
            var Q2;
            Q2=makeQuery(id+"F16.imprint","IMPRINT",FACE,{"disambiguationData":[TD([[makeQuery(id+"F16.imprint","IMPRINT",EDGE,{"derivedFrom":sQuery(id+"F16.wireOp",EDGE,"E91.MirrorC")}),1.0]])]});
            var Q3;
            Q3=makeQuery(id+"F2.opExtrude","CAP_FACE",FACE,{"disambiguationData":[OSD([sQuery(id+"F0.wireOp",EDGE,"E12"),sQuery(id+"F0.wireOp",EDGE,"E13"),sQuery(id+"F0.wireOp",EDGE,"E14"),sQuery(id+"F0.wireOp",EDGE,"E15"),sQuery(id+"F0.wireOp",EDGE,"E17.filletArc"),sQuery(id+"F0.wireOp",EDGE,"E18.filletArc"),sQuery(id+"F0.wireOp",EDGE,"E19.filletArc"),sQuery(id+"F0.wireOp",EDGE,"E20.filletArc"),sQuery(id+"F0.wireOp",EDGE,"E25.0"),sQuery(id+"F0.wireOp",EDGE,"E25.1"),sQuery(id+"F0.wireOp",EDGE,"E25.2"),sQuery(id+"F0.wireOp",EDGE,"E25.3"),sQuery(id+"F0.wireOp",EDGE,"E25.4"),sQuery(id+"F0.wireOp",EDGE,"E25.5"),sQuery(id+"F0.wireOp",EDGE,"E25.6"),sQuery(id+"F0.wireOp",EDGE,"E25.7")])],"isStart":false});
            extrude(context, id + "F17", {"entities" : qUnion([Q0, Q1, Q2]), "endBound" : BoundingType.UP_TO_SURFACE, "depth" : 25 * mm, "endBoundEntityFace" : qUnion([Q3]), "offsetDistance" : 25 * mm});
        }
    });
